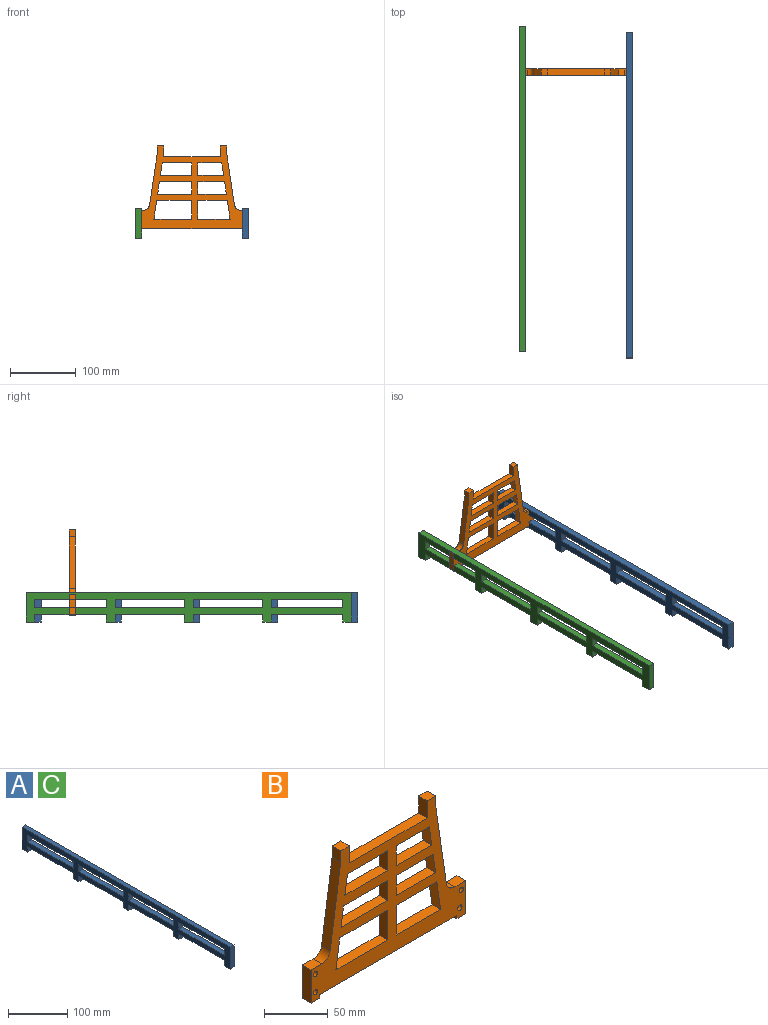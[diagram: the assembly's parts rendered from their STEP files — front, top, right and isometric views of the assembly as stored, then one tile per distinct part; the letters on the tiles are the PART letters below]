
ASSEMBLY  parts=3 mates=1
PART A: 38 faces, bbox 9.5x496.1x45 mm
  f0: plane 105.75x9.53mm, normal (0,0,-1), area 1007.3mm2, adj f1,f35,f36,f37
  f1: plane 13.5x9.53mm, normal (0,-1,0), area 128.6mm2, adj f0,f2,f36,f37
  f2: plane 105.75x9.53mm, normal (0,0,1), area 1007.3mm2, adj f1,f35,f36,f37
  f3: plane 108.53x9.53mm, normal (0,0,-1), area 1033.8mm2, adj f4,f31,f36,f37
  f4: plane 13.5x9.53mm, normal (0,-1,0), area 128.6mm2, adj f3,f5,f36,f37
  f5: plane 108.53x9.53mm, normal (0,0,1), area 1033.8mm2, adj f4,f31,f36,f37
  f6: plane 11.5x9.53mm, normal (0,-1,0), area 109.5mm2, adj f7,f32,f36,f37
  f7: plane 13.5x9.53mm, normal (0,0,-1), area 128.6mm2, adj f6,f8,f36,f37
  f8: plane 11.5x9.53mm, normal (0,1,0), area 109.5mm2, adj f7,f9,f36,f37
  f9: plane 108.53x9.53mm, normal (0,0,-1), area 1033.8mm2, adj f8,f10,f36,f37
  f10: plane 11.5x9.53mm, normal (0,-1,0), area 109.5mm2, adj f9,f11,f36,f37
  f11: plane 13.5x9.53mm, normal (0,0,-1), area 128.6mm2, adj f10,f12,f36,f37
  f12: plane 45x9.53mm, normal (0,1,0), area 428.6mm2, adj f11,f13,f36,f37
  f13: plane 496.06x9.53mm, normal (0,0,1), area 4725mm2, adj f12,f14,f36,f37
  f14: plane 45x9.53mm, normal (0,-1,0), area 428.6mm2, adj f13,f15,f36,f37
  f15: plane 13.5x9.53mm, normal (0,0,-1), area 128.6mm2, adj f14,f16,f36,f37
  f16: plane 11.5x9.53mm, normal (0,1,0), area 109.5mm2, adj f15,f17,f36,f37
  f17: plane 108.53x9.53mm, normal (0,0,-1), area 1033.8mm2, adj f16,f18,f36,f37
  f18: plane 11.5x9.53mm, normal (0,-1,0), area 109.5mm2, adj f17,f19,f36,f37
  f19: plane 13.5x9.53mm, normal (0,0,-1), area 128.6mm2, adj f18,f20,f36,f37
  f20: plane 11.5x9.53mm, normal (0,1,0), area 109.5mm2, adj f19,f21,f36,f37
  f21: plane 105.75x9.53mm, normal (0,0,-1), area 1007.3mm2, adj f20,f22,f36,f37
  f22: plane 11.5x9.53mm, normal (0,-1,0), area 109.5mm2, adj f21,f23,f36,f37
  f23: plane 13.5x9.53mm, normal (0,0,-1), area 128.6mm2, adj f22,f24,f36,f37
  f24: plane 11.5x9.53mm, normal (0,1,0), area 109.5mm2, adj f23,f32,f36,f37
  f25: plane 13.5x9.53mm, normal (0,1,0), area 128.6mm2, adj f26,f33,f36,f37
  f26: plane 108.53x9.53mm, normal (0,0,-1), area 1033.8mm2, adj f25,f27,f36,f37
  f27: plane 13.5x9.53mm, normal (0,-1,0), area 128.6mm2, adj f26,f33,f36,f37
  f28: plane 13.5x9.53mm, normal (0,1,0), area 128.6mm2, adj f29,f34,f36,f37
  f29: plane 105.75x9.53mm, normal (0,0,-1), area 1007.3mm2, adj f28,f30,f36,f37
  f30: plane 13.5x9.53mm, normal (0,-1,0), area 128.6mm2, adj f29,f34,f36,f37
  f31: plane 13.5x9.53mm, normal (0,1,0), area 128.6mm2, adj f3,f5,f36,f37
  f32: plane 105.75x9.53mm, normal (0,0,-1), area 1007.3mm2, adj f6,f24,f36,f37
  f33: plane 108.53x9.53mm, normal (0,0,1), area 1033.8mm2, adj f25,f27,f36,f37
  f34: plane 105.75x9.53mm, normal (0,0,1), area 1007.3mm2, adj f28,f30,f36,f37
  f35: plane 13.5x9.53mm, normal (0,1,0), area 128.6mm2, adj f0,f2,f36,f37
  f36: plane 496.06x45mm, normal (1,0,0), area 11608.8mm2, adj f0,f1,f2,f3,f4,f5,f6,f7
  f37: plane 496.06x45mm, normal (-1,0,0), area 11608.8mm2, adj f0,f1,f2,f3,f4,f5,f6,f7
PART B: 50 faces, bbox 171.5x9.5x129.7 mm
  f0: plane 19.05x9.53mm, normal (-1,0,0), area 181.5mm2, adj f1,f47,f48,f49
  f1: plane 51.81x9.53mm, normal (0,0,1), area 493.5mm2, adj f0,f2,f48,f49
  f2: plane 19.05x9.53mm, normal (0.99,0,-0.15), area 183.4mm2, adj f1,f47,f48,f49
  f3: plane 47.59x9.53mm, normal (0,0,1), area 453.3mm2, adj f4,f37,f48,f49
  f4: plane 19.05x9.53mm, normal (0.99,0,-0.15), area 183.4mm2, adj f3,f5,f48,f49
  f5: plane 44.77x9.53mm, normal (0,0,-1), area 426.4mm2, adj f4,f37,f48,f49
  f6: plane 31.75x9.53mm, normal (1,0,0), area 302.4mm2, adj f7,f38,f48,f49
  f7: plane 11.85x9.53mm, normal (0,0,1), area 112.8mm2, adj f6,f8,f48,f49
  f8: cylinder r=9.53mm len=9.53mm, axis (0,1,0), area 129.2mm2, adj f7,f9,f48,f49
  f9: plane 79.19x11.71mm, normal (0.99,0,0.15), area 762.5mm2, adj f8,f10,f48,f49
  f10: plane 10.58x9.53mm, normal (1,0,0), area 100.8mm2, adj f9,f11,f48,f49
  f11: plane 9.53x9.53mm, normal (0,0,1), area 90.7mm2, adj f10,f12,f48,f49
  f12: plane 16.41x9.53mm, normal (-1,0,0), area 156.3mm2, adj f11,f13,f48,f49
  f13: plane 86.47x9.53mm, normal (0,0,1), area 823.6mm2, adj f12,f14,f48,f49
  f14: plane 16.41x9.53mm, normal (1,0,0), area 156.3mm2, adj f13,f15,f48,f49
  f15: plane 9.53x9.53mm, normal (0,0,1), area 90.7mm2, adj f14,f16,f48,f49
  f16: plane 10.58x9.53mm, normal (-1,0,0), area 100.8mm2, adj f15,f17,f48,f49
  f17: plane 79.19x11.71mm, normal (-0.99,0,0.15), area 762.5mm2, adj f16,f18,f48,f49
  f18: cylinder r=9.53mm len=9.53mm, axis (0,1,0), area 129.2mm2, adj f17,f19,f48,f49
  f19: plane 11.85x9.53mm, normal (0,0,1), area 112.8mm2, adj f18,f20,f48,f49
  f20: plane 31.75x9.53mm, normal (-1,0,0), area 302.4mm2, adj f19,f21,f48,f49
  f21: plane 9.53x9.53mm, normal (0,0,-1), area 90.7mm2, adj f20,f22,f48,f49
  f22: plane 9.53x3.18mm, normal (1,0,0), area 30.2mm2, adj f21,f23,f48,f49
  f23: plane 152.42x9.53mm, normal (0,0,-1), area 1451.8mm2, adj f22,f24,f48,f49
  f24: plane 9.53x3.18mm, normal (-1,0,0), area 30.2mm2, adj f23,f38,f48,f49
  f25: plane 57.44x9.53mm, normal (0,0,1), area 547.1mm2, adj f26,f39,f48,f49
  f26: plane 28.58x9.53mm, normal (0.99,0,-0.15), area 275.1mm2, adj f25,f27,f48,f49
  f27: plane 53.22x9.53mm, normal (0,0,-1), area 506.9mm2, adj f26,f39,f48,f49
  f28: plane 28.58x9.53mm, normal (1,0,0), area 272.2mm2, adj f29,f40,f48,f49
  f29: plane 44.95x9.53mm, normal (0,0,-1), area 428.2mm2, adj f28,f30,f48,f49
  f30: plane 28.58x9.53mm, normal (-0.99,0,-0.15), area 275.1mm2, adj f29,f40,f48,f49
  f31: plane 19.05x9.53mm, normal (-0.99,0,-0.15), area 183.4mm2, adj f32,f41,f48,f49
  f32: plane 39.32x9.53mm, normal (0,0,1), area 374.5mm2, adj f31,f33,f48,f49
  f33: plane 19.05x9.53mm, normal (1,0,0), area 181.5mm2, adj f32,f41,f48,f49
  f34: plane 43.54x9.53mm, normal (0,0,1), area 414.7mm2, adj f35,f42,f48,f49
  f35: plane 19.05x9.53mm, normal (1,0,0), area 181.5mm2, adj f34,f36,f48,f49
  f36: plane 40.73x9.53mm, normal (0,0,-1), area 387.9mm2, adj f35,f42,f48,f49
  f37: plane 19.05x9.53mm, normal (-1,0,0), area 181.5mm2, adj f3,f5,f48,f49
  f38: plane 9.53x9.53mm, normal (0,0,-1), area 90.7mm2, adj f6,f24,f48,f49
  f39: plane 28.58x9.53mm, normal (-1,0,0), area 272.2mm2, adj f25,f27,f48,f49
  f40: plane 49.18x9.53mm, normal (0,0,1), area 468.4mm2, adj f28,f30,f48,f49
  f41: plane 36.5x9.53mm, normal (0,0,-1), area 347.7mm2, adj f31,f33,f48,f49
  f42: plane 19.05x9.53mm, normal (-0.99,0,-0.15), area 183.4mm2, adj f34,f36,f48,f49
  f43: cylinder r=2.38mm len=9.53mm, axis (0,1,0), area 142.5mm2, adj f48,f49
  f44: cylinder r=2.38mm len=9.53mm, axis (0,1,0), area 142.5mm2, adj f48,f49
  f45: cylinder r=2.38mm len=9.53mm, axis (0,1,0), area 142.5mm2, adj f48,f49
  f46: cylinder r=2.38mm len=9.53mm, axis (0,1,0), area 142.5mm2, adj f48,f49
  f47: plane 48.99x9.53mm, normal (0,0,-1), area 466.7mm2, adj f0,f2,f48,f49
  f48: plane 171.47x129.66mm, normal (0,-1,0), area 8665.7mm2, adj f0,f1,f2,f3,f4,f5,f6,f7
  f49: plane 171.47x129.66mm, normal (0,1,0), area 8665.7mm2, adj f0,f1,f2,f3,f4,f5,f6,f7
PART C: same geometry as A
PLACE A t=(221,-103.53,-30)mm
PLACE B t=(144.79,88.56,-11.02)mm
PLACE C t=(59.06,-94,-30)mm
MATE planar C.f37 <-> B.f20  axis (-1,0,0) through (59.06,-342.03,-13.25)mm
